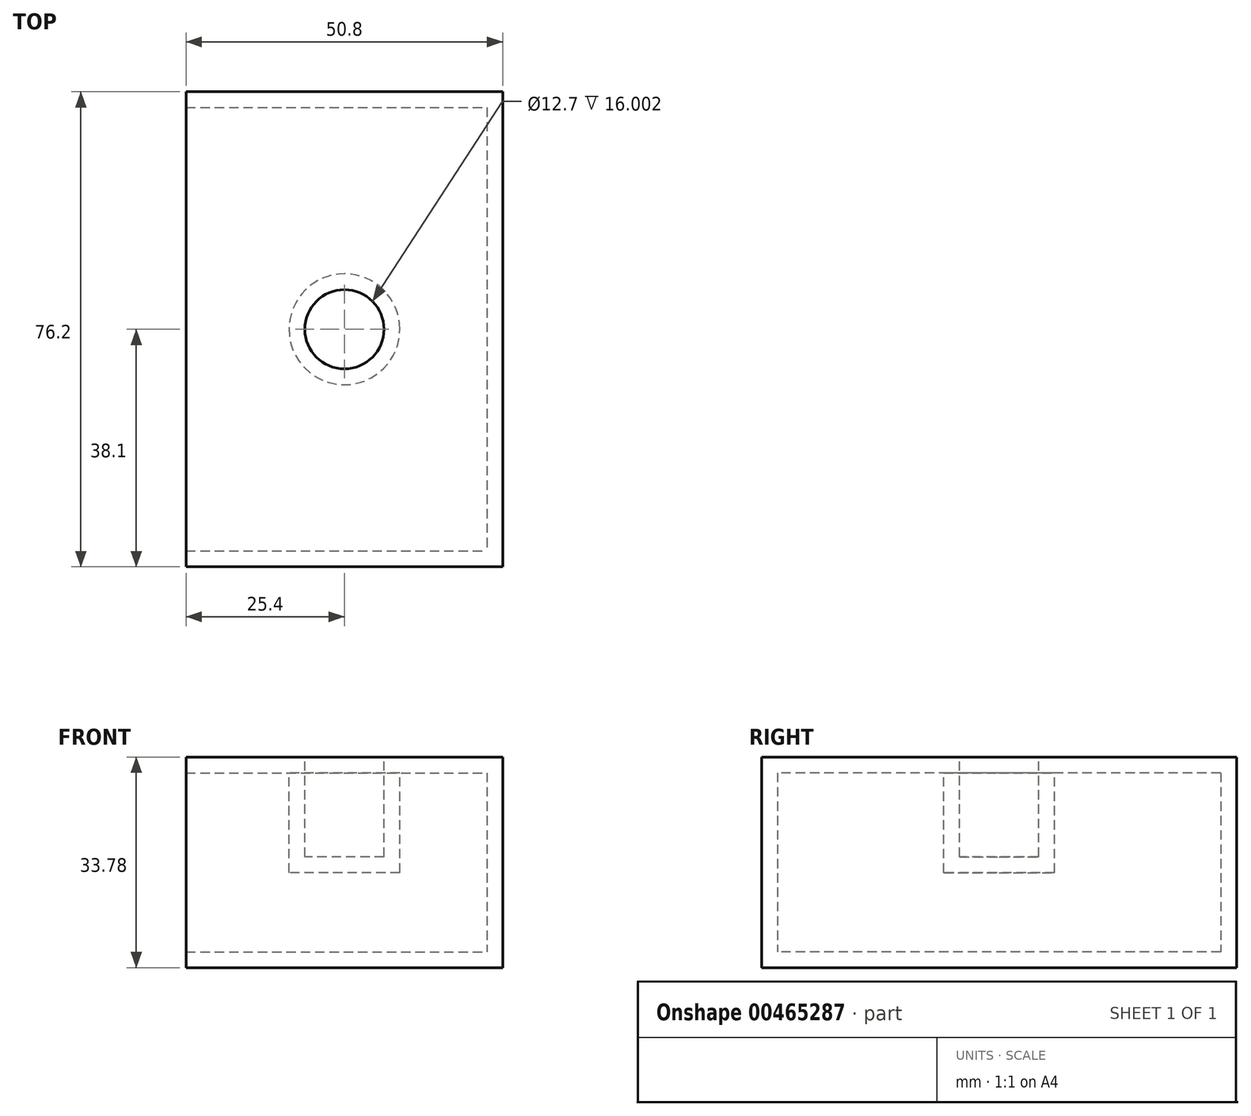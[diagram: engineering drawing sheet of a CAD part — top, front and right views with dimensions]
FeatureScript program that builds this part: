
annotation { "Feature Type Name" : "Feature", "Feature Type Description" : "" }
export const myFeature = defineFeature(function(context is Context, id is Id, definition is map)
    precondition{}
    {
        {
            var Q0;
            Q0=qCreatedBy(makeId("Top.planeOp"),FACE);
            var sketch = newSketch(context, id + "F0", { "sketchPlane" : qUnion([Q0])});
            skLineSegment(sketch, "E0.bottom", {"start": v(0, 76.2) * mm, "end": v(50.8, 76.2) * mm});
            skLineSegment(sketch, "E0.top", {"start": v(0, 0) * mm, "end": v(50.8, 0) * mm});
            skLineSegment(sketch, "E0.left", {"start": v(0, 76.2) * mm, "end": v(0, 0) * mm});
            skLineSegment(sketch, "E0.right", {"start": v(50.8, 76.2) * mm, "end": v(50.8, 0) * mm});
            skLineSegment(sketch, "E1", {"start": v(50.8, 76.2) * mm, "end": v(0, 0) * mm, "construction": true});
            skSolve(sketch);
        }
        {
            var Q0;
            Q0=makeQuery(id+"F0.imprint","IMPRINT",FACE,{"disambiguationData":[TD([[makeQuery(id+"F0.imprint","IMPRINT",EDGE,{"derivedFrom":sQuery(id+"F0.wireOp",EDGE,"E0.bottom")}),-1.0]])]});
            extrude(context, id + "F1", {"entities" : qUnion([Q0]), "depth" : 33.78 * mm});
        }
        {
            var Q0;
            Q0=makeQuery(id+"F1.opExtrude","CAP_FACE",FACE,{"disambiguationData":[OSD([sQuery(id+"F0.wireOp",EDGE,"E0.bottom"),sQuery(id+"F0.wireOp",EDGE,"E0.top"),sQuery(id+"F0.wireOp",EDGE,"E0.left"),sQuery(id+"F0.wireOp",EDGE,"E0.right")])],"isStart":false});
            var sketch = newSketch(context, id + "F2", { "sketchPlane" : qUnion([Q0])});
            skCircle(sketch, "E2", {"center": v(25.4, 38.1) * mm, "radius": 6.35 * mm});
            skLineSegment(sketch, "E3", {"start": v(0, 0) * mm, "end": v(50.8, 76.2) * mm, "construction": true});
            skSolve(sketch);
        }
        {
            var Q0;
            Q0=makeQuery(id+"F2.imprint","IMPRINT",FACE,{"disambiguationData":[TD([[makeQuery(id+"F2.imprint","IMPRINT",EDGE,{"derivedFrom":sQuery(id+"F2.wireOp",EDGE,"E2")}),1.0]])]});
            extrude(context, id + "F3", {"entities" : qUnion([Q0]), "operationType" : NewBodyOperationType.REMOVE, "oppositeDirection" : true, "depth" : 16 * mm});
        }
        {
            var Q0;
            Q0=makeQuery(id+"F1.opExtrude","SWEPT_FACE",FACE,{"disambiguationData":[OSD([sQuery(id+"F0.wireOp",EDGE,"E0.left")])]});
            shell(context, id + "F4", {"entities" : qUnion([Q0]), "thickness" : 2.54 * mm});
        }
    });
